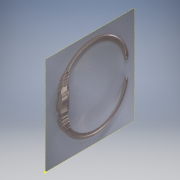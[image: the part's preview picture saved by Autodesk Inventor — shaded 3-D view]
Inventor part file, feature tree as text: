
AUTODESK INVENTOR PART (.ipt)
format: ipt  version: 2019 (Build 230136000, 136)  size: 401,920 bytes
history: native  units: mm
features: sketch x1, other x1
ambient origin geometry x8: Origin, YZ Plane, XZ Plane, XY Plane, X Axis, Y Axis, Z Axis, Center Point
feature tree (2):
  sketch  "Skizze1"
  other  "Bild1"
